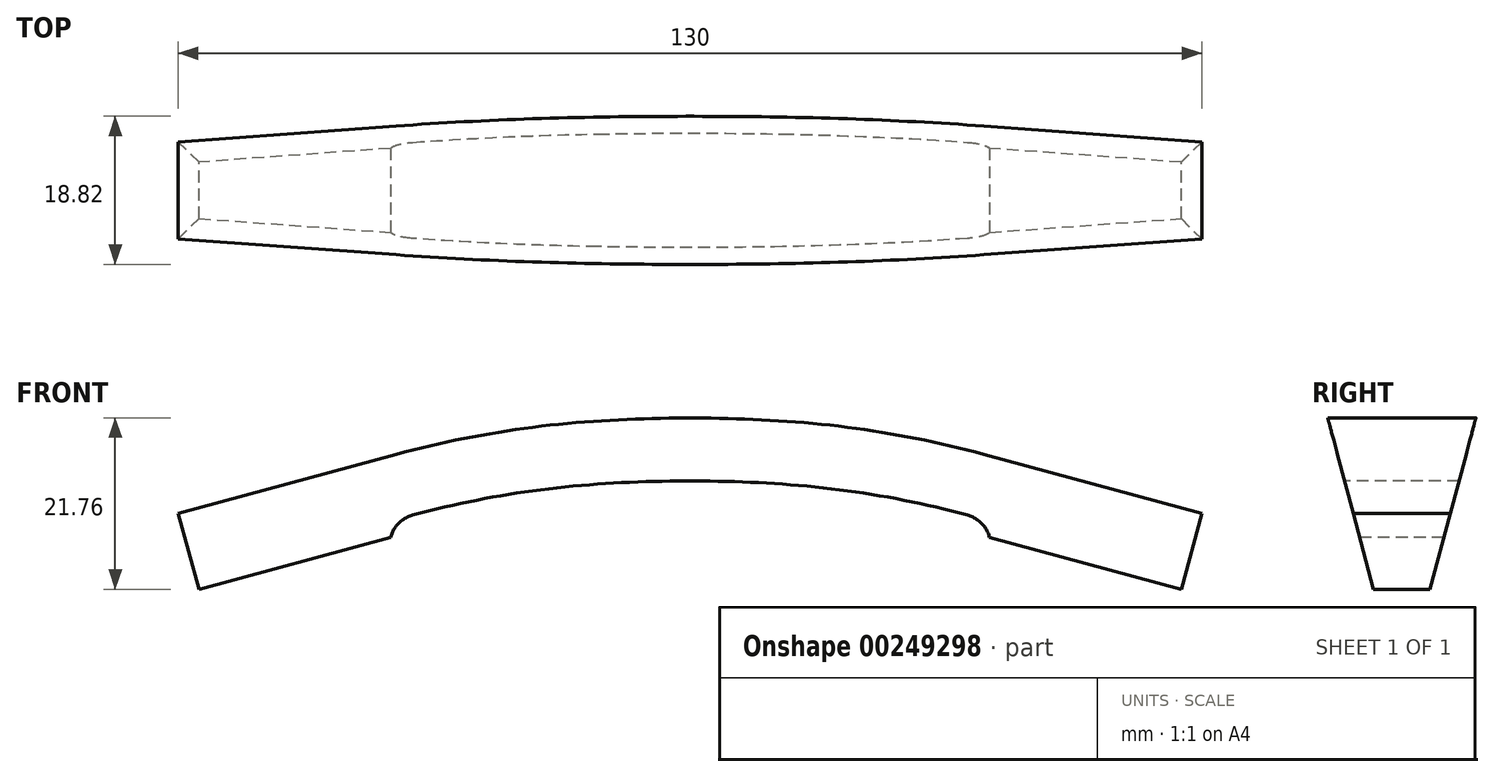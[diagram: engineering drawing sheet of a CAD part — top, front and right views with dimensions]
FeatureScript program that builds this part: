
annotation { "Feature Type Name" : "Feature", "Feature Type Description" : "" }
export const myFeature = defineFeature(function(context is Context, id is Id, definition is map)
    precondition{}
    {
        {
            var Q0;
            Q0=qCreatedBy(makeId("Front.planeOp"),FACE);
            var sketch = newSketch(context, id + "F0", { "sketchPlane" : qUnion([Q0])});
            skLineSegment(sketch, "E0", {"start": v(-50, 26.25) * mm, "end": v(-40, 28.56) * mm, "construction": true});
            skLineSegment(sketch, "E1", {"start": v(50, 26.25) * mm, "end": v(40, 28.56) * mm, "construction": true});
            skArc(sketch, "E2", {"start": v(40, 28.56) * mm, "mid": v(0, 33.12) * mm, "end": v(-40, 28.56) * mm, "construction": true});
            skLineSegment(sketch, "E3", {"start": v(-50, 26.25) * mm, "end": v(-50, 24.25) * mm, "construction": true});
            skLineSegment(sketch, "E4", {"start": v(50, 26.25) * mm, "end": v(50, 24.25) * mm, "construction": true});
            skArc(sketch, "E5.0", {"start": v(12.28, 34.7) * mm, "mid": v(0, 35.12) * mm, "end": v(-12.28, 34.7) * mm});
            skArc(sketch, "E6.0", {"start": v(11.6, 24.72) * mm, "mid": v(0, 25.12) * mm, "end": v(-11.6, 24.72) * mm});
            skLineSegment(sketch, "E7", {"start": v(34.7, 20.84) * mm, "end": v(62.4, 13.36) * mm});
            skLineSegment(sketch, "E8", {"start": v(62.4, 13.36) * mm, "end": v(65, 23.02) * mm});
            skLineSegment(sketch, "E9", {"start": v(65, 23.02) * mm, "end": v(37.32, 30.5) * mm});
            skLineSegment(sketch, "E10", {"start": v(-65, 23.02) * mm, "end": v(-62.4, 13.36) * mm});
            skLineSegment(sketch, "E11", {"start": v(-65, 23.02) * mm, "end": v(-37.32, 30.5) * mm});
            skLineSegment(sketch, "E12", {"start": v(-62.4, 13.36) * mm, "end": v(-34.7, 20.84) * mm});
            skPoint(sketch, "E13.visualSharp", {"position": v(-28.85, 32.79) * mm});
            skArc(sketch, "E13.filletArc", {"start": v(-12.28, 34.7) * mm, "mid": v(-24.9, 33.21) * mm, "end": v(-37.32, 30.5) * mm});
            skPoint(sketch, "E14.visualSharp", {"position": v(28.85, 32.79) * mm});
            skArc(sketch, "E14.filletArc", {"start": v(37.32, 30.5) * mm, "mid": v(24.9, 33.21) * mm, "end": v(12.28, 34.7) * mm});
            skPoint(sketch, "E15.visualSharp", {"position": v(-26.74, 23) * mm});
            skArc(sketch, "E15.filletArc", {"start": v(-11.6, 24.72) * mm, "mid": v(-23.25, 23.35) * mm, "end": v(-34.7, 20.84) * mm});
            skPoint(sketch, "E16.visualSharp", {"position": v(26.74, 23) * mm});
            skArc(sketch, "E16.filletArc", {"start": v(34.7, 20.84) * mm, "mid": v(23.25, 23.35) * mm, "end": v(11.6, 24.72) * mm});
            skLineSegment(sketch, "E17.0", {"start": v(63.7, 18.2) * mm, "end": v(36.01, 25.67) * mm, "construction": true});
            skLineSegment(sketch, "E17.1", {"start": v(-63.7, 18.2) * mm, "end": v(-36.01, 25.67) * mm, "construction": true});
            skArc(sketch, "E17.2", {"start": v(-11.94, 29.7) * mm, "mid": v(-24.08, 28.28) * mm, "end": v(-36.01, 25.67) * mm, "construction": true});
            skArc(sketch, "E17.3", {"start": v(11.94, 29.7) * mm, "mid": v(0, 30.12) * mm, "end": v(-11.94, 29.7) * mm, "construction": true});
            skArc(sketch, "E17.4", {"start": v(36.01, 25.67) * mm, "mid": v(24.08, 28.28) * mm, "end": v(11.94, 29.7) * mm, "construction": true});
            skSolve(sketch);
        }
        {
            var Q0;
            Q0=makeQuery(id+"F0.imprint","IMPRINT",FACE,{"disambiguationData":[TD([[makeQuery(id+"F0.imprint","IMPRINT",EDGE,{"derivedFrom":sQuery(id+"F0.wireOp",EDGE,"E5.0")}),1.0]])]});
            extrude(context, id + "F1", {"entities" : qUnion([Q0]), "depth" : 30 * mm, "offsetDistance" : 25 * mm, "symmetric" : true});
        }
        {
            var Q0;
            Q0=qCreatedBy(makeId("Right.planeOp"),FACE);
            var sketch = newSketch(context, id + "F2", { "sketchPlane" : qUnion([Q0])});
            skLineSegment(sketch, "E18", {"start": v(0, 0) * mm, "end": v(-17, 63.44) * mm, "construction": true});
            skLineSegment(sketch, "E19", {"start": v(-17, 63.44) * mm, "end": v(-17, 0) * mm});
            skLineSegment(sketch, "E20", {"start": v(-17, 0) * mm, "end": v(0, 0) * mm});
            skLineSegment(sketch, "E21", {"start": v(0, 0) * mm, "end": v(17, 63.44) * mm, "construction": true});
            skLineSegment(sketch, "E22", {"start": v(17, 63.44) * mm, "end": v(17, 0) * mm});
            skLineSegment(sketch, "E23", {"start": v(17, 0) * mm, "end": v(0, 0) * mm});
            skLineSegment(sketch, "E24", {"start": v(-17, 63.44) * mm, "end": v(-1.88, 7) * mm});
            skLineSegment(sketch, "E25", {"start": v(-1.88, 7) * mm, "end": v(1.88, 7) * mm});
            skLineSegment(sketch, "E26", {"start": v(1.88, 7) * mm, "end": v(17, 63.44) * mm});
            skSolve(sketch);
        }
        {
            var Q0;
            Q0=makeQuery(id+"F2.imprint","IMPRINT",FACE,{"disambiguationData":[TD([[makeQuery(id+"F2.imprint","IMPRINT",EDGE,{"derivedFrom":sQuery(id+"F2.wireOp",EDGE,"E19")}),1.0]])]});
            extrude(context, id + "F3", {"entities" : qUnion([Q0]), "operationType" : NewBodyOperationType.REMOVE, "oppositeDirection" : true, "depth" : 200 * mm, "offsetDistance" : 25 * mm, "symmetric" : true});
        }
        {
            var Q0;
            Q0=qCreatedBy(makeId("Front.planeOp"),FACE);
            var sketch = newSketch(context, id + "F4", { "sketchPlane" : qUnion([Q0])});
            skArc(sketch, "E27.0", {"start": v(-11.74, 26.72) * mm, "mid": v(-23.58, 25.32) * mm, "end": v(-35.23, 22.78) * mm});
            skArc(sketch, "E28.0", {"start": v(11.74, 26.72) * mm, "mid": v(0, 27.12) * mm, "end": v(-11.74, 26.72) * mm});
            skArc(sketch, "E29.0", {"start": v(35.23, 22.78) * mm, "mid": v(23.58, 25.32) * mm, "end": v(11.74, 26.72) * mm});
            skLineSegment(sketch, "E30.0", {"start": v(-38.05, 19.94) * mm, "end": v(-34.7, 20.84) * mm});
            skArc(sketch, "E31.0", {"start": v(-11.6, 24.72) * mm, "mid": v(-23.25, 23.35) * mm, "end": v(-34.7, 20.84) * mm});
            skArc(sketch, "E32.0", {"start": v(11.6, 24.72) * mm, "mid": v(0, 25.12) * mm, "end": v(-11.6, 24.72) * mm});
            skArc(sketch, "E33.0", {"start": v(34.7, 20.84) * mm, "mid": v(23.25, 23.35) * mm, "end": v(11.6, 24.72) * mm});
            skLineSegment(sketch, "E34.0", {"start": v(34.7, 20.84) * mm, "end": v(38.05, 19.94) * mm});
            skPoint(sketch, "E35.orphan", {"position": v(-62.4, 13.36) * mm});
            skPoint(sketch, "E36.orphan", {"position": v(62.4, 13.36) * mm});
            skArc(sketch, "E37", {"start": v(-35.23, 22.78) * mm, "mid": v(-37.02, 21.74) * mm, "end": v(-38.05, 19.94) * mm});
            skArc(sketch, "E38", {"start": v(38.05, 19.94) * mm, "mid": v(37.02, 21.74) * mm, "end": v(35.23, 22.78) * mm});
            skSolve(sketch);
        }
        {
            var Q0;
            Q0=makeQuery(id+"F4.imprint","IMPRINT",FACE,{"disambiguationData":[TD([[makeQuery(id+"F4.imprint","IMPRINT",EDGE,{"derivedFrom":sQuery(id+"F4.wireOp",EDGE,"E27.0")}),1.0]])]});
            extrude(context, id + "F5", {"entities" : qUnion([Q0]), "operationType" : NewBodyOperationType.REMOVE, "oppositeDirection" : true, "depth" : 25 * mm, "offsetDistance" : 25 * mm, "symmetric" : true});
        }
    });
